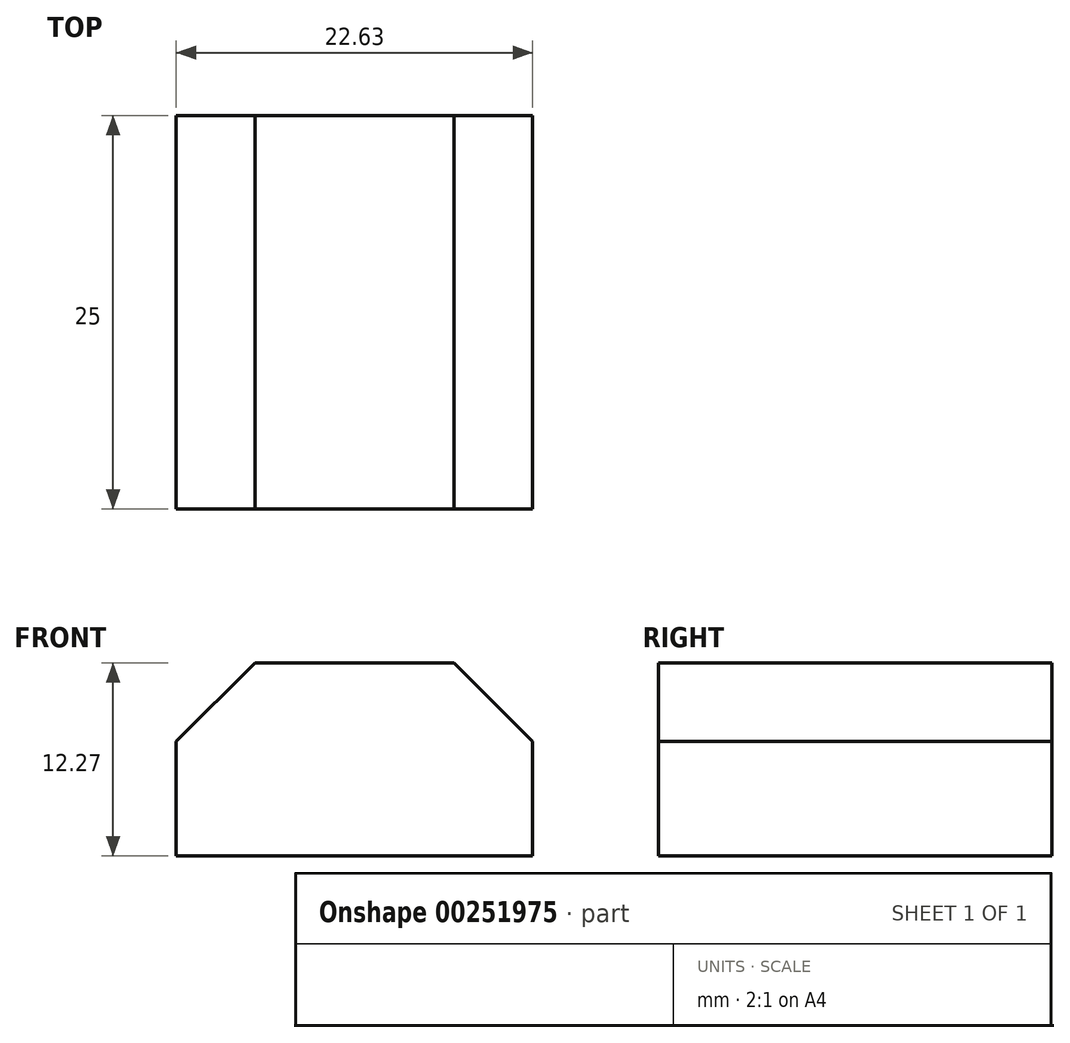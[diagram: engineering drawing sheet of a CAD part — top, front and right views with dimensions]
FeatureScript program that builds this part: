
annotation { "Feature Type Name" : "Feature", "Feature Type Description" : "" }
export const myFeature = defineFeature(function(context is Context, id is Id, definition is map)
    precondition{}
    {
        {
            var Q0;
            Q0=qCreatedBy(makeId("Front.planeOp"),FACE);
            var sketch = newSketch(context, id + "F0", { "sketchPlane" : qUnion([Q0])});
            skLineSegment(sketch, "E0.bottom", {"start": v(0, 0) * mm, "end": v(22.63, 0) * mm});
            skLineSegment(sketch, "E0.top", {"start": v(0, -12.27) * mm, "end": v(22.63, -12.27) * mm});
            skLineSegment(sketch, "E0.left", {"start": v(0, 0) * mm, "end": v(0, -12.27) * mm});
            skLineSegment(sketch, "E0.right", {"start": v(22.63, 0) * mm, "end": v(22.63, -12.27) * mm});
            skLineSegment(sketch, "E1.bottom", {"start": v(0, 0) * mm, "end": v(-9.4, 0) * mm});
            skLineSegment(sketch, "E1.top", {"start": v(0, -12.27) * mm, "end": v(-9.4, -12.27) * mm});
            skLineSegment(sketch, "E1.right", {"start": v(-9.4, 0) * mm, "end": v(-9.4, -12.27) * mm});
            skLineSegment(sketch, "E2.top", {"start": v(0, -28.4) * mm, "end": v(22.63, -28.4) * mm});
            skLineSegment(sketch, "E2.left", {"start": v(0, -12.27) * mm, "end": v(0, -28.4) * mm});
            skLineSegment(sketch, "E2.right", {"start": v(22.63, -12.27) * mm, "end": v(22.63, -28.4) * mm});
            skSolve(sketch);
        }
        {
            var Q0;
            Q0=makeQuery(id+"F0.imprint","IMPRINT",FACE,{"disambiguationData":[TD([[makeQuery(id+"F0.imprint","IMPRINT",EDGE,{"derivedFrom":sQuery(id+"F0.wireOp",EDGE,"E0.bottom")}),-1.0]])]});
            extrude(context, id + "F1", {"entities" : qUnion([Q0]), "depth" : 25 * mm});
        }
        {
            var Q0;
            Q0=qCreatedBy(makeId("Top.planeOp"),FACE);
            var sketch = newSketch(context, id + "F2", { "sketchPlane" : qUnion([Q0])});
            skCircle(sketch, "E3", {"center": v(-79.23, 19.02) * mm, "radius": 22.3 * mm});
            skSolve(sketch);
        }
        {
            var Q0;
            Q0=makeQuery(id+"F2.imprint","IMPRINT",FACE,{"disambiguationData":[TD([[makeQuery(id+"F2.imprint","IMPRINT",EDGE,{"derivedFrom":sQuery(id+"F2.wireOp",EDGE,"E3")}),1.0]])]});
            extrude(context, id + "F3", {"entities" : qUnion([Q0]), "depth" : 29.9 * mm});
        }
        {
            var Q0;
            Q0=makeQuery(id+"F3.opExtrude","SWEPT_BODY",BODY,{"disambiguationData":[OSD([sQuery(id+"F2.wireOp",EDGE,"E3")])]});
            deleteBodies(context, id + "F4", {"entities" : qUnion([Q0])});
        }
        {
            var Q0;
            Q0=makeQuery(id+"F1.opExtrude","SWEPT_EDGE",EDGE,{"disambiguationData":[OSD([sQuery(id+"F0.wireOp",EDGE,"E0.bottom"),sQuery(id+"F0.wireOp",EDGE,"E0.right")])]});
            chamfer(context, id + "F5", {"entities" : qUnion([Q0]), "width" : 5 * mm, "tangentPropagation" : true});
        }
        {
            var Q0;
            Q0=makeQuery(id+"F1.opExtrude","SWEPT_EDGE",EDGE,{"disambiguationData":[OSD([sQuery(id+"F0.wireOp",EDGE,"E0.bottom"),sQuery(id+"F0.wireOp",EDGE,"E1.bottom"),sQuery(id+"F0.wireOp",EDGE,"E0.left")])]});
            chamfer(context, id + "F6", {"entities" : qUnion([Q0]), "width" : 5 * mm, "tangentPropagation" : true});
        }
    });
